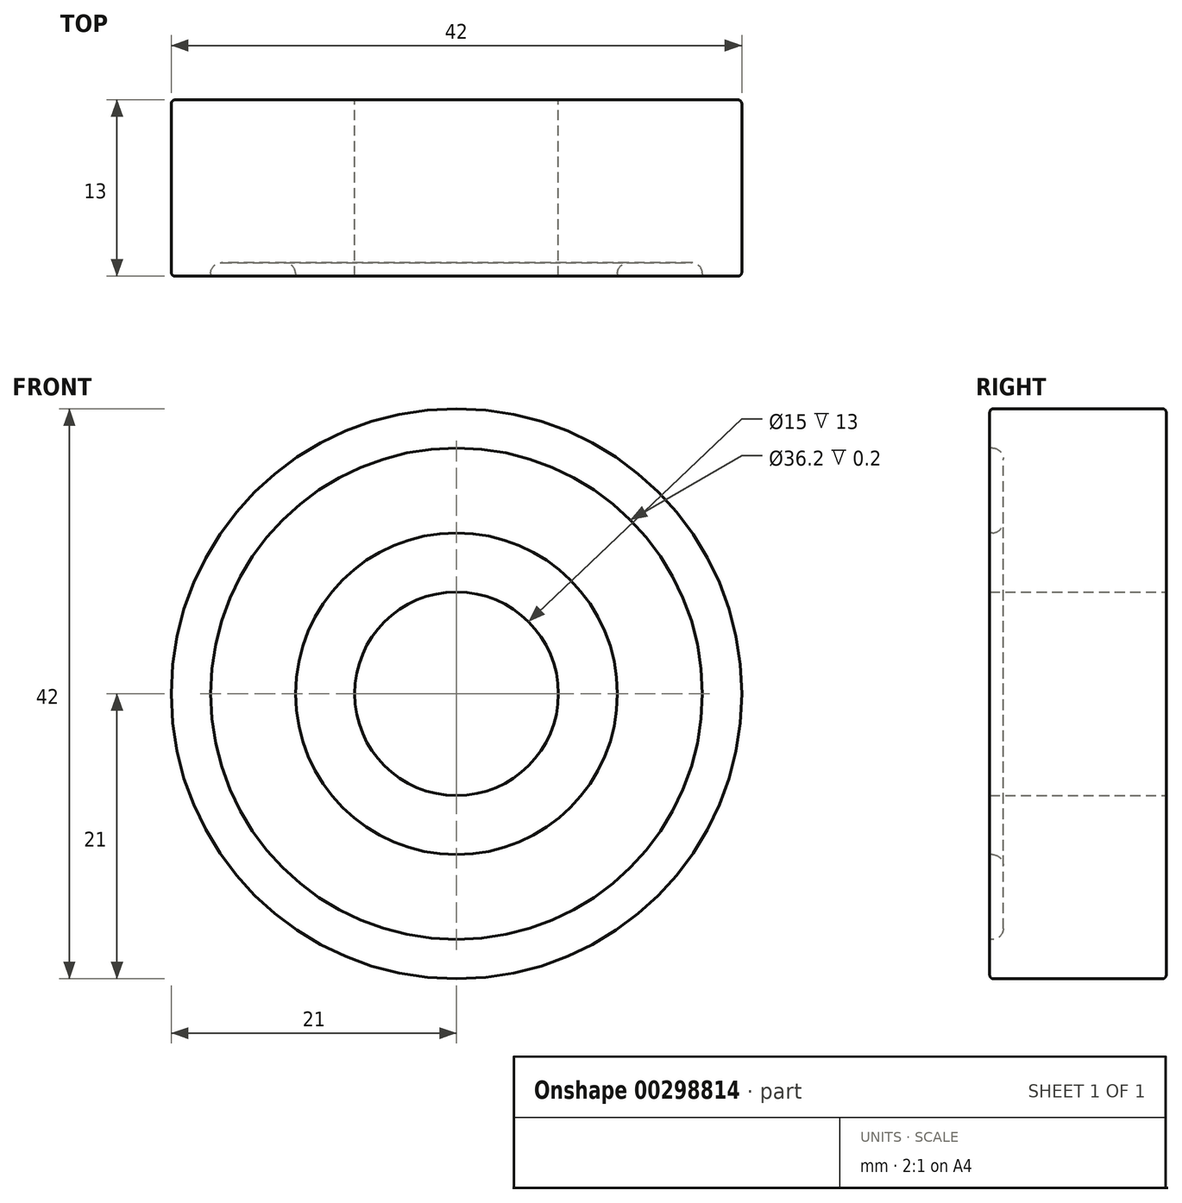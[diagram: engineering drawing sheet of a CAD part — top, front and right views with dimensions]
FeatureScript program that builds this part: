
annotation { "Feature Type Name" : "Feature", "Feature Type Description" : "" }
export const myFeature = defineFeature(function(context is Context, id is Id, definition is map)
    precondition{}
    {
        {
            var Q0;
            Q0=qCreatedBy(makeId("Front.planeOp"),FACE);
            var sketch = newSketch(context, id + "F0", { "sketchPlane" : qUnion([Q0])});
            skCircle(sketch, "E0", {"center": v(0, 0) * mm, "radius": 7.5 * mm});
            skCircle(sketch, "E1", {"center": v(0, 0) * mm, "radius": 21 * mm});
            skSolve(sketch);
        }
        {
            var Q0;
            Q0=makeQuery(id+"F0.imprint","IMPRINT",FACE,{"disambiguationData":[TD([[makeQuery(id+"F0.imprint","IMPRINT",EDGE,{"derivedFrom":sQuery(id+"F0.wireOp",EDGE,"E0")}),-1.0]])]});
            extrude(context, id + "F1", {"entities" : qUnion([Q0]), "depth" : 6.5 * mm, "hasSecondDirection" : true, "secondDirectionOppositeDirection" : true, "secondDirectionDepth" : 6.5 * mm});
        }
        {
            var Q0;
            Q0=makeQuery(id+"F1.opExtrude","CAP_FACE",FACE,{"disambiguationData":[OSD([sQuery(id+"F0.wireOp",EDGE,"E0"),sQuery(id+"F0.wireOp",EDGE,"E1")])],"isStart":false});
            var sketch = newSketch(context, id + "F2", { "sketchPlane" : qUnion([Q0])});
            skCircle(sketch, "E2", {"center": v(0, 0) * mm, "radius": 11.85 * mm});
            skCircle(sketch, "E3", {"center": v(0, 0) * mm, "radius": 18.1 * mm});
            skSolve(sketch);
        }
        {
            var Q0;
            Q0=makeQuery(id+"F2.imprint","IMPRINT",FACE,{"disambiguationData":[TD([[makeQuery(id+"F2.imprint","IMPRINT",EDGE,{"derivedFrom":sQuery(id+"F2.wireOp",EDGE,"E2")}),-1.0]])]});
            extrude(context, id + "F3", {"entities" : qUnion([Q0]), "operationType" : NewBodyOperationType.REMOVE, "oppositeDirection" : true, "depth" : 1 * mm});
        }
        {
            var Q0;
            Q0=makeQuery(id+"FZNNnHi4Xex2cEG_1.1.F3.boolean.opBoolean","COPY",EDGE,{"derivedFrom":makeQuery(id+"FZNNnHi4Xex2cEG_1.1.F3.opExtrude","CAP_EDGE",EDGE,{"disambiguationData":[OSD([sQuery(id+"F2.wireOp",EDGE,"E3")])],"isStart":false})});
            var Q1;
            Q1=makeQuery(id+"FZNNnHi4Xex2cEG_1.1.F3.boolean.opBoolean","COPY",EDGE,{"derivedFrom":makeQuery(id+"FZNNnHi4Xex2cEG_1.1.F3.opExtrude","CAP_EDGE",EDGE,{"disambiguationData":[OSD([sQuery(id+"F2.wireOp",EDGE,"E2")])],"isStart":false})});
            var Q2;
            Q2=makeQuery(id+"F3.boolean.opBoolean","COPY",EDGE,{"derivedFrom":makeQuery(id+"F3.opExtrude","CAP_EDGE",EDGE,{"disambiguationData":[OSD([sQuery(id+"F2.wireOp",EDGE,"E2")])],"isStart":false})});
            var Q3;
            Q3=makeQuery(id+"F3.boolean.opBoolean","COPY",EDGE,{"derivedFrom":makeQuery(id+"F3.opExtrude","CAP_EDGE",EDGE,{"disambiguationData":[OSD([sQuery(id+"F2.wireOp",EDGE,"E3")])],"isStart":false})});
            fillet(context, id + "F4", {"entities" : qUnion([Q0, Q1, Q2, Q3]), "radius" : 0.8 * mm, "tangentPropagation" : true, "allowEdgeOverflow" : false});
        }
        {
            var Q0;
            Q0=makeQuery(id+"F3.boolean.opBoolean","COPY",EDGE,{"derivedFrom":makeQuery(id+"F3.opExtrude","CAP_EDGE",EDGE,{"disambiguationData":[OSD([sQuery(id+"F2.wireOp",EDGE,"E3")])],"isStart":true})});
            var Q1;
            Q1=makeQuery(id+"F1.opExtrude","CAP_EDGE",EDGE,{"disambiguationData":[OSD([sQuery(id+"F0.wireOp",EDGE,"E1")])],"isStart":false});
            var Q2;
            Q2=makeQuery(id+"F3.boolean.opBoolean","COPY",EDGE,{"derivedFrom":makeQuery(id+"F3.opExtrude","CAP_EDGE",EDGE,{"disambiguationData":[OSD([sQuery(id+"F2.wireOp",EDGE,"E2")])],"isStart":true})});
            var Q3;
            Q3=makeQuery(id+"F1.opExtrude","CAP_EDGE",EDGE,{"disambiguationData":[OSD([sQuery(id+"F0.wireOp",EDGE,"E1")])],"isStart":true});
            var Q4;
            Q4=makeQuery(id+"FZNNnHi4Xex2cEG_1.1.F3.boolean.opBoolean","COPY",EDGE,{"derivedFrom":makeQuery(id+"FZNNnHi4Xex2cEG_1.1.F3.opExtrude","CAP_EDGE",EDGE,{"disambiguationData":[OSD([sQuery(id+"F2.wireOp",EDGE,"E3")])],"isStart":true})});
            var Q5;
            Q5=makeQuery(id+"FZNNnHi4Xex2cEG_1.1.F3.boolean.opBoolean","COPY",EDGE,{"derivedFrom":makeQuery(id+"FZNNnHi4Xex2cEG_1.1.F3.opExtrude","CAP_EDGE",EDGE,{"disambiguationData":[OSD([sQuery(id+"F2.wireOp",EDGE,"E2")])],"isStart":true})});
            fillet(context, id + "F5", {"entities" : qUnion([Q0, Q1, Q2, Q3, Q4, Q5]), "radius" : 0.3 * mm, "tangentPropagation" : true, "allowEdgeOverflow" : false});
        }
    });
